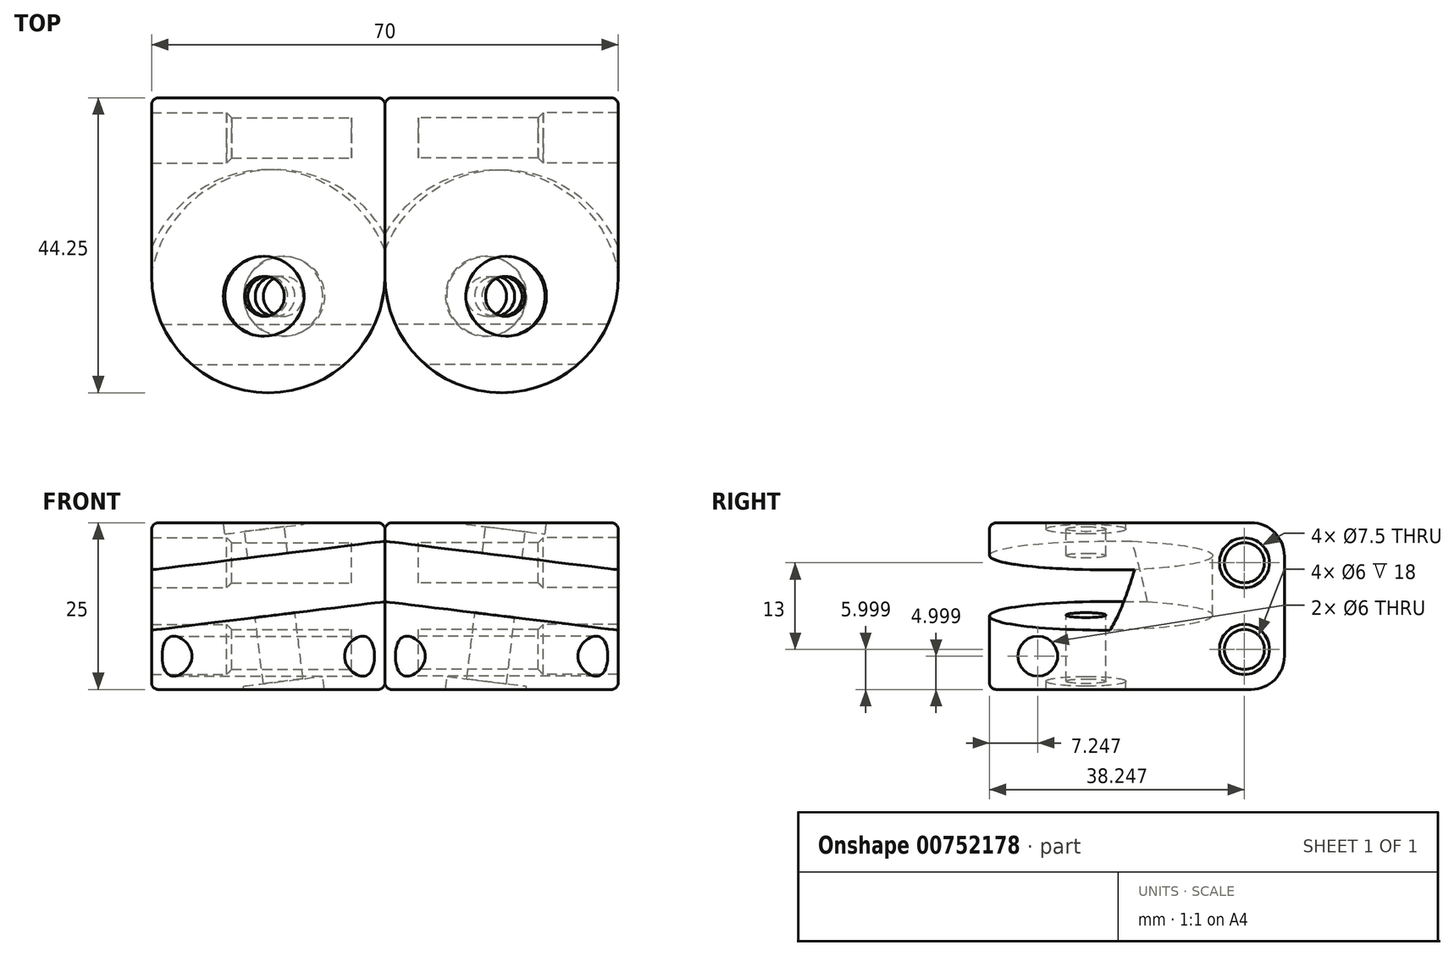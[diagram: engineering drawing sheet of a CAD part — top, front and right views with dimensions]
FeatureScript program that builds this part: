
annotation { "Feature Type Name" : "Feature", "Feature Type Description" : "" }
export const myFeature = defineFeature(function(context is Context, id is Id, definition is map)
    precondition{}
    {
        {
            var Q0;
            Q0=qCreatedBy(makeId("Right.planeOp"),FACE);
            var sketch = newSketch(context, id + "F0", { "sketchPlane" : qUnion([Q0])});
            skLineSegment(sketch, "E0.bottom", {"start": v(-22.23, 10.8) * mm, "end": v(17.77, 10.8) * mm});
            skLineSegment(sketch, "E0.top", {"start": v(-22.23, -14.2) * mm, "end": v(17.77, -14.2) * mm});
            skLineSegment(sketch, "E0.left", {"start": v(-22.23, 10.8) * mm, "end": v(-22.23, -14.2) * mm});
            skLineSegment(sketch, "E0.right", {"start": v(22.77, 5.8) * mm, "end": v(22.77, -9.2) * mm});
            skCircle(sketch, "E1", {"center": v(16.77, 4.8) * mm, "radius": 3 * mm});
            skCircle(sketch, "E2", {"center": v(16.77, -8.2) * mm, "radius": 3 * mm});
            skPoint(sketch, "E3.visualSharp", {"position": v(22.77, 10.8) * mm});
            skArc(sketch, "E3.filletArc", {"start": v(22.77, 5.8) * mm, "mid": v(21.3, 9.33) * mm, "end": v(17.77, 10.8) * mm});
            skPoint(sketch, "E4.visualSharp", {"position": v(22.77, -14.2) * mm});
            skArc(sketch, "E4.filletArc", {"start": v(17.77, -14.2) * mm, "mid": v(21.3, -12.74) * mm, "end": v(22.77, -9.2) * mm});
            skCircle(sketch, "E5", {"center": v(16.77, 4.8) * mm, "radius": 3.75 * mm});
            skCircle(sketch, "E6", {"center": v(16.77, -8.2) * mm, "radius": 3.75 * mm});
            skCircle(sketch, "E7", {"center": v(-14.23, -9.2) * mm, "radius": 3 * mm});
            skSolve(sketch);
        }
        {
            var Q0;
            Q0=makeQuery(id+"F0.imprint","IMPRINT",FACE,{"disambiguationData":[TD([[makeQuery(id+"F0.imprint","IMPRINT",EDGE,{"derivedFrom":sQuery(id+"F0.wireOp",EDGE,"E0.bottom")}),-1.0]])]});
            extrude(context, id + "F1", {"entities" : qUnion([Q0]), "depth" : 35 * mm, "offsetDistance" : 25 * mm});
        }
        {
            var Q0;
            Q0=makeQuery(id+"F0.imprint","IMPRINT",FACE,{"disambiguationData":[TD([[makeQuery(id+"F0.imprint","IMPRINT",EDGE,{"derivedFrom":sQuery(id+"F0.wireOp",EDGE,"E1")}),-1.0]])]});
            var Q1;
            Q1=makeQuery(id+"F0.imprint","IMPRINT",FACE,{"disambiguationData":[TD([[makeQuery(id+"F0.imprint","IMPRINT",EDGE,{"derivedFrom":sQuery(id+"F0.wireOp",EDGE,"E2")}),-1.0]])]});
            extrude(context, id + "F2", {"entities" : qUnion([Q0, Q1]), "operationType" : NewBodyOperationType.ADD, "depth" : 25 * mm, "offsetDistance" : 25 * mm});
        }
        {
            var Q0;
            Q0=qCreatedBy(makeId("Top.planeOp"),FACE);
            var sketch = newSketch(context, id + "F3", { "sketchPlane" : qUnion([Q0])});
            skCircle(sketch, "E8", {"center": v(17.5, -3.98) * mm, "radius": 17.5 * mm});
            skLineSegment(sketch, "E9", {"start": v(0, 0) * mm, "end": v(0, -26.83) * mm});
            skLineSegment(sketch, "E10", {"start": v(0, -26.83) * mm, "end": v(35, -26.83) * mm});
            skLineSegment(sketch, "E11", {"start": v(35, -26.83) * mm, "end": v(35, 5.67) * mm});
            skSolve(sketch);
        }
        {
            var Q0;
            Q0=qCreatedBy(makeId("Top.planeOp"),FACE);
            var Q1;
            Q1=makeQuery(id+"F1.opExtrude","CAP_EDGE",EDGE,{"disambiguationData":[OSD([sQuery(id+"F0.wireOp",EDGE,"E0.bottom")])],"isStart":false});
            cPlane(context, id + "F4", {"entities" : qUnion([Q0, Q1]), "cplaneType" : CPlaneType.LINE_ANGLE, "offset" : 25 * mm, "angle" : 7 * degree, "width" : 150 * mm, "height" : 150 * mm});
        }
        {
            var Q0;
            {var subQ5=sQuery(id+"F3.wireOp",EDGE,"E10");Q0=makeQuery(id+"F3.imprint","IMPRINT",FACE,{"disambiguationData":[TD([[makeQuery(id+"F3.imprint","IMPRINT",EDGE,{"derivedFrom":subQ5}),1.0]])]});}
            extrude(context, id + "F5", {"entities" : qUnion([Q0]), "operationType" : NewBodyOperationType.REMOVE, "oppositeDirection" : true, "depth" : 25 * mm, "offsetDistance" : 25 * mm, "hasSecondDirection" : true, "secondDirectionOppositeDirection" : false, "secondDirectionDepth" : 25 * mm});
        }
        {
            var Q0;
            Q0=makeQuery(id+"F0.imprint","IMPRINT",FACE,{"disambiguationData":[TD([[makeQuery(id+"F0.imprint","IMPRINT",EDGE,{"derivedFrom":sQuery(id+"F0.wireOp",EDGE,"E1")}),1.0]])]});
            var Q1;
            Q1=makeQuery(id+"F0.imprint","IMPRINT",FACE,{"disambiguationData":[TD([[makeQuery(id+"F0.imprint","IMPRINT",EDGE,{"derivedFrom":sQuery(id+"F0.wireOp",EDGE,"E2")}),1.0]])]});
            extrude(context, id + "F6", {"entities" : qUnion([Q0, Q1]), "operationType" : NewBodyOperationType.ADD, "depth" : 5 * mm, "offsetDistance" : 25 * mm});
        }
        {
            var Q0;
            Q0=qCreatedBy(id+"F4.planeOp",FACE);
            var sketch = newSketch(context, id + "F7", { "sketchPlane" : qUnion([Q0])});
            skCircle(sketch, "E12", {"center": v(16.73, 7) * mm, "radius": 19 * mm});
            skLineSegment(sketch, "E13", {"start": v(0, 0) * mm, "end": v(0, -24.2) * mm});
            skLineSegment(sketch, "E14", {"start": v(0, -24.2) * mm, "end": v(35.73, -24.2) * mm});
            skLineSegment(sketch, "E15", {"start": v(35.73, -24.2) * mm, "end": v(35.73, 0) * mm});
            skCircle(sketch, "E16", {"center": v(16.73, 7) * mm, "radius": 3 * mm});
            skCircle(sketch, "E17", {"center": v(16.73, 7) * mm, "radius": 6 * mm});
            skSolve(sketch);
        }
        {
            var Q0;
            Q0=makeQuery(id+"F7.imprint","IMPRINT",FACE,{"disambiguationData":[TD([[makeQuery(id+"F7.imprint","IMPRINT",EDGE,{"derivedFrom":sQuery(id+"F7.wireOp",EDGE,"E12")}),1.0]])]});
            var Q1;
            Q1=makeQuery(id+"F7.imprint","IMPRINT",FACE,{"disambiguationData":[TD([[makeQuery(id+"F7.imprint","IMPRINT",EDGE,{"derivedFrom":sQuery(id+"F7.wireOp",EDGE,"E16")}),-1.0]])]});
            var Q2;
            Q2=makeQuery(id+"F7.imprint","IMPRINT",FACE,{"disambiguationData":[TD([[makeQuery(id+"F7.imprint","IMPRINT",EDGE,{"derivedFrom":sQuery(id+"F7.wireOp",EDGE,"E16")}),1.0]])]});
            extrude(context, id + "F8", {"entities" : qUnion([Q0, Q1, Q2]), "operationType" : NewBodyOperationType.REMOVE, "depth" : 16 * mm, "offsetDistance" : 25 * mm, "hasSecondDirection" : true, "secondDirectionOppositeDirection" : false, "secondDirectionDepth" : 7 * mm});
        }
        {
            var Q0;
            Q0=makeQuery(id+"FIWJNFuMKNCfMLk_1.boolean.opBoolean","INTERSECT",EDGE,{"derivedFrom":[makeQuery(id+"F1.opExtrude","SWEPT_FACE",FACE,{"disambiguationData":[OSD([sQuery(id+"F0.wireOp",EDGE,"E0.top")])]}),makeQuery(id+"FIWJNFuMKNCfMLk_1.opExtrude","SWEPT_FACE",FACE,{"disambiguationData":[OSD([sQuery(id+"F7.wireOp",EDGE,"E12")])]})]});
            var Q1;
            Q1=makeQuery(id+"F1.opExtrude","CAP_EDGE",EDGE,{"disambiguationData":[OSD([sQuery(id+"F0.wireOp",EDGE,"E0.top")])],"isStart":true});
            var Q2;
            Q2=makeQuery(id+"F1.opExtrude","CAP_EDGE",EDGE,{"disambiguationData":[OSD([sQuery(id+"F0.wireOp",EDGE,"E0.top")])],"isStart":false});
            var Q3;
            Q3=makeQuery(id+"F1.opExtrude","CAP_EDGE",EDGE,{"disambiguationData":[OSD([sQuery(id+"F0.wireOp",EDGE,"E4.filletArc")])],"isStart":true});
            var Q4;
            Q4=makeQuery(id+"F1.opExtrude","CAP_EDGE",EDGE,{"disambiguationData":[OSD([sQuery(id+"F0.wireOp",EDGE,"E4.filletArc")])],"isStart":false});
            var Q5;
            Q5=makeQuery(id+"F1.opExtrude","CAP_EDGE",EDGE,{"disambiguationData":[OSD([sQuery(id+"F0.wireOp",EDGE,"E0.right")])],"isStart":false});
            var Q6;
            Q6=makeQuery(id+"F1.opExtrude","CAP_EDGE",EDGE,{"disambiguationData":[OSD([sQuery(id+"F0.wireOp",EDGE,"E3.filletArc")])],"isStart":false});
            var Q7;
            Q7=makeQuery(id+"F1.opExtrude","CAP_EDGE",EDGE,{"disambiguationData":[OSD([sQuery(id+"F0.wireOp",EDGE,"E0.bottom")])],"isStart":false});
            var Q8;
            Q8=makeQuery(id+"F1.opExtrude","CAP_EDGE",EDGE,{"disambiguationData":[OSD([sQuery(id+"F0.wireOp",EDGE,"E0.bottom")])],"isStart":true});
            var Q9;
            Q9=makeQuery(id+"F1.opExtrude","CAP_EDGE",EDGE,{"disambiguationData":[OSD([sQuery(id+"F0.wireOp",EDGE,"E3.filletArc")])],"isStart":true});
            var Q10;
            Q10=makeQuery(id+"F1.opExtrude","CAP_EDGE",EDGE,{"disambiguationData":[OSD([sQuery(id+"F0.wireOp",EDGE,"E0.right")])],"isStart":true});
            fillet(context, id + "F9", {"entities" : qUnion([Q0, Q1, Q2, Q3, Q4, Q5, Q6, Q7, Q8, Q9, Q10]), "radius" : 1 * mm, "tangentPropagation" : true, "allowEdgeOverflow" : false});
        }
        {
            var Q0;
            Q0=makeQuery(id+"F2.opExtrude","CAP_EDGE",EDGE,{"disambiguationData":[OSD([sQuery(id+"F0.wireOp",EDGE,"E1")])],"isStart":false});
            var Q1;
            Q1=makeQuery(id+"F2.opExtrude","CAP_EDGE",EDGE,{"disambiguationData":[OSD([sQuery(id+"F0.wireOp",EDGE,"E2")])],"isStart":false});
            chamfer(context, id + "F10", {"entities" : qUnion([Q0, Q1]), "width" : 2 * mm, "tangentPropagation" : true});
        }
        {
            var Q0;
            Q0=makeQuery(id+"F7.imprint","IMPRINT",FACE,{"disambiguationData":[TD([[makeQuery(id+"F7.imprint","IMPRINT",EDGE,{"derivedFrom":sQuery(id+"F7.wireOp",EDGE,"E16")}),1.0]])]});
            extrude(context, id + "F11", {"entities" : qUnion([Q0]), "operationType" : NewBodyOperationType.REMOVE, "endBound" : BoundingType.THROUGH_ALL, "depth" : 25 * mm, "offsetDistance" : 25 * mm});
        }
        {
            var Q0;
            Q0=makeQuery(id+"F7.imprint","IMPRINT",FACE,{"disambiguationData":[TD([[makeQuery(id+"F7.imprint","IMPRINT",EDGE,{"derivedFrom":sQuery(id+"F7.wireOp",EDGE,"E16")}),-1.0]])]});
            extrude(context, id + "F12", {"entities" : qUnion([Q0]), "operationType" : NewBodyOperationType.REMOVE, "depth" : 3 * mm, "offsetDistance" : 25 * mm});
        }
        {
            var Q0;
            Q0=makeQuery(id+"F7.imprint","IMPRINT",FACE,{"disambiguationData":[TD([[makeQuery(id+"F7.imprint","IMPRINT",EDGE,{"derivedFrom":sQuery(id+"F7.wireOp",EDGE,"E16")}),-1.0]])]});
            extrude(context, id + "F13", {"entities" : qUnion([Q0]), "operationType" : NewBodyOperationType.REMOVE, "depth" : 40 * mm, "offsetDistance" : 25 * mm, "hasSecondDirection" : true, "secondDirectionOppositeDirection" : false, "secondDirectionDepth" : 26 * mm});
        }
        {
            var Q0;
            Q0=makeQuery(id+"F1.opExtrude","SWEPT_BODY",BODY,{"disambiguationData":[OSD([sQuery(id+"F0.wireOp",EDGE,"E0.bottom"),sQuery(id+"F0.wireOp",EDGE,"E0.top"),sQuery(id+"F0.wireOp",EDGE,"E0.left"),sQuery(id+"F0.wireOp",EDGE,"E0.right"),sQuery(id+"F0.wireOp",EDGE,"E3.filletArc"),sQuery(id+"F0.wireOp",EDGE,"E4.filletArc"),sQuery(id+"F0.wireOp",EDGE,"E5"),sQuery(id+"F0.wireOp",EDGE,"E6"),sQuery(id+"F0.wireOp",EDGE,"E7")])]});
            var Q1;
            Q1=qCreatedBy(makeId("Right.planeOp"),FACE);
            mirror(context, id + "F14", {"entities" : qUnion([Q0]), "mirrorPlane" : qUnion([Q1])});
        }
    });
